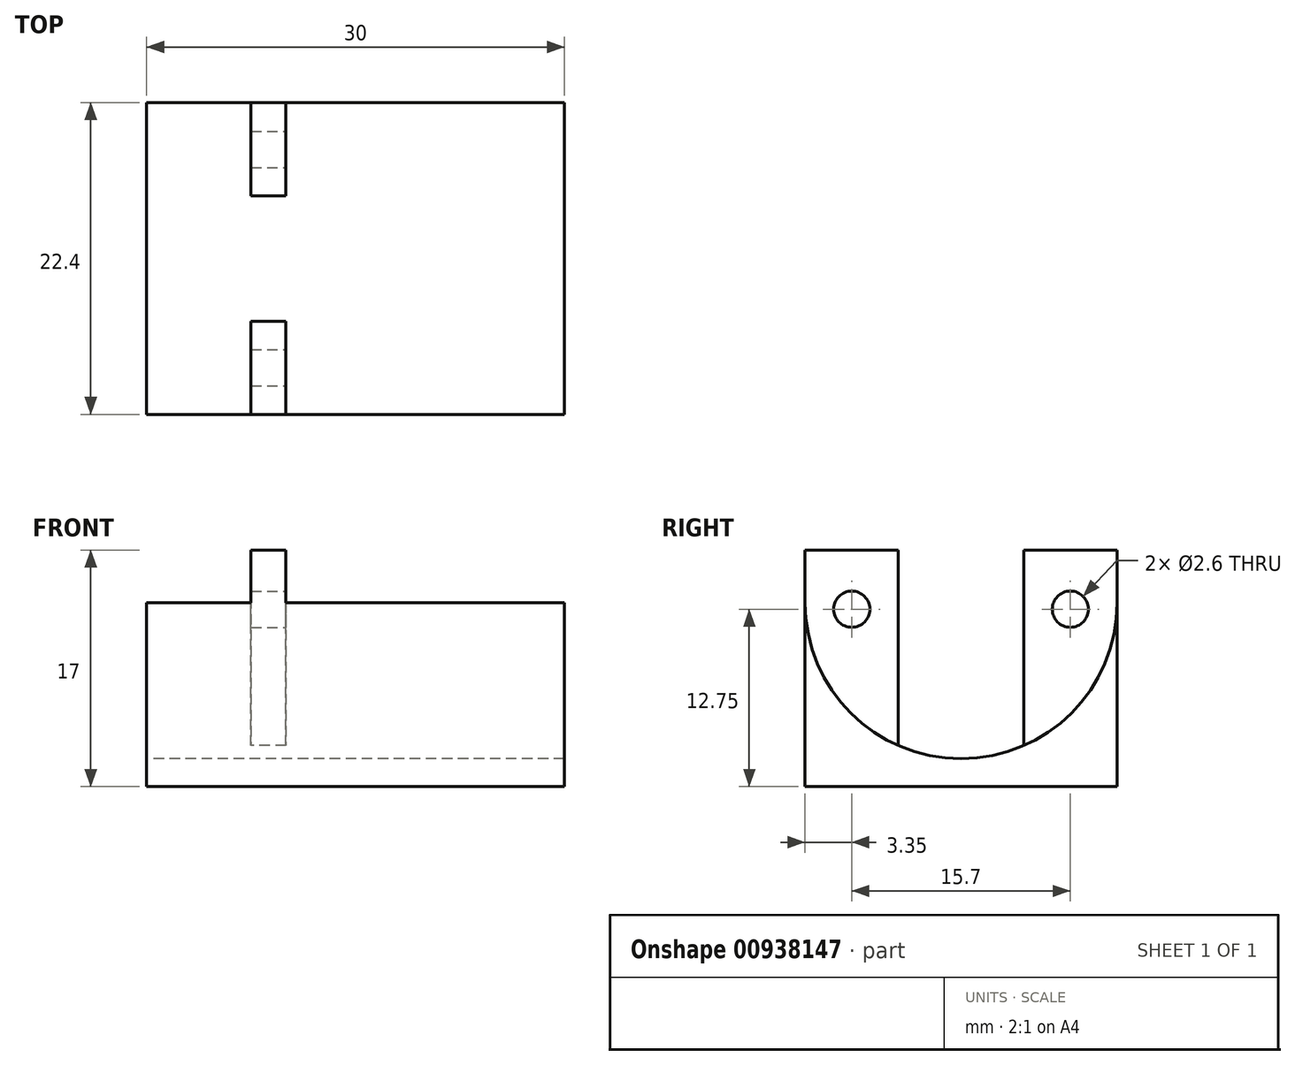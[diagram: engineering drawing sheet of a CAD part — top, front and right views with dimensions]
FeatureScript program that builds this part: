
annotation { "Feature Type Name" : "Feature", "Feature Type Description" : "" }
export const myFeature = defineFeature(function(context is Context, id is Id, definition is map)
    precondition{}
    {
        {
            var Q0;
            Q0=qCreatedBy(makeId("Right.planeOp"),FACE);
            var sketch = newSketch(context, id + "F0", { "sketchPlane" : qUnion([Q0])});
            skLineSegment(sketch, "E0", {"start": v(-11.2, -13.2) * mm, "end": v(11.2, -13.2) * mm});
            skLineSegment(sketch, "E1", {"start": v(11.2, -13.2) * mm, "end": v(11.2, 0) * mm});
            skLineSegment(sketch, "E2", {"start": v(-11.2, -13.2) * mm, "end": v(-11.2, 0) * mm});
            skPoint(sketch, "E3", {"position": v(0, -13.2) * mm});
            skArc(sketch, "E4", {"start": v(-11.2, 0) * mm, "mid": v(0, -11.2) * mm, "end": v(11.2, 0) * mm});
            skSolve(sketch);
        }
        {
            var Q0;
            Q0=makeQuery(id+"F0.imprint","IMPRINT",FACE,{"disambiguationData":[TD([[makeQuery(id+"F0.imprint","IMPRINT",EDGE,{"derivedFrom":sQuery(id+"F0.wireOp",EDGE,"E0")}),1.0]])]});
            extrude(context, id + "F1", {"entities" : qUnion([Q0]), "depth" : 30 * mm, "offsetDistance" : 25 * mm});
        }
        {
            var Q0;
            Q0=makeQuery(id+"F1.opExtrude","SWEPT_FACE",FACE,{"disambiguationData":[OSD([sQuery(id+"F0.wireOp",EDGE,"E0")])]});
            var sketch = newSketch(context, id + "F2", { "sketchPlane" : qUnion([Q0])});
            skLineSegment(sketch, "E5.bottom", {"start": v(10, -11.2) * mm, "end": v(7.5, -11.2) * mm});
            skLineSegment(sketch, "E5.top", {"start": v(10, -4.5) * mm, "end": v(7.5, -4.5) * mm});
            skLineSegment(sketch, "E5.left", {"start": v(10, -11.2) * mm, "end": v(10, -4.5) * mm});
            skLineSegment(sketch, "E5.right", {"start": v(7.5, -11.2) * mm, "end": v(7.5, -4.5) * mm});
            skLineSegment(sketch, "E6.bottom", {"start": v(10, 11.2) * mm, "end": v(7.5, 11.2) * mm});
            skLineSegment(sketch, "E6.top", {"start": v(10, 4.5) * mm, "end": v(7.5, 4.5) * mm});
            skLineSegment(sketch, "E6.left", {"start": v(10, 11.2) * mm, "end": v(10, 4.5) * mm});
            skLineSegment(sketch, "E6.right", {"start": v(7.5, 11.2) * mm, "end": v(7.5, 4.5) * mm});
            skSolve(sketch);
        }
        {
            var Q0;
            Q0=makeQuery(id+"F2.imprint","IMPRINT",FACE,{"disambiguationData":[TD([[makeQuery(id+"F2.imprint","IMPRINT",EDGE,{"derivedFrom":sQuery(id+"F2.wireOp",EDGE,"E6.bottom")}),1.0]])]});
            var Q1;
            Q1=makeQuery(id+"F2.imprint","IMPRINT",FACE,{"disambiguationData":[TD([[makeQuery(id+"F2.imprint","IMPRINT",EDGE,{"derivedFrom":sQuery(id+"F2.wireOp",EDGE,"E5.bottom")}),-1.0]])]});
            extrude(context, id + "F3", {"entities" : qUnion([Q0, Q1]), "operationType" : NewBodyOperationType.ADD, "oppositeDirection" : true, "depth" : 2 * mm + 15 * mm, "offsetDistance" : 25 * mm});
        }
        {
            var Q0;
            Q0=makeQuery(id+"F3.opExtrude","SWEPT_FACE",FACE,{"disambiguationData":[OSD([sQuery(id+"F2.wireOp",EDGE,"E6.left")])]});
            var sketch = newSketch(context, id + "F4", { "sketchPlane" : qUnion([Q0])});
            skCircle(sketch, "E7", {"center": v(-7.85, -0.45) * mm, "radius": 1.3 * mm});
            skCircle(sketch, "E8", {"center": v(7.85, -0.45) * mm, "radius": 1.3 * mm});
            skSolve(sketch);
        }
        {
            var Q0;
            Q0=makeQuery(id+"F4.imprint","IMPRINT",FACE,{"disambiguationData":[TD([[makeQuery(id+"F4.imprint","IMPRINT",EDGE,{"derivedFrom":sQuery(id+"F4.wireOp",EDGE,"E7")}),1.0]])]});
            var Q1;
            Q1=makeQuery(id+"F4.imprint","IMPRINT",FACE,{"disambiguationData":[TD([[makeQuery(id+"F4.imprint","IMPRINT",EDGE,{"derivedFrom":sQuery(id+"F4.wireOp",EDGE,"E8")}),1.0]])]});
            extrude(context, id + "F5", {"entities" : qUnion([Q0, Q1]), "operationType" : NewBodyOperationType.REMOVE, "endBound" : BoundingType.THROUGH_ALL, "oppositeDirection" : true, "depth" : 25 * mm, "offsetDistance" : 25 * mm});
        }
    });
